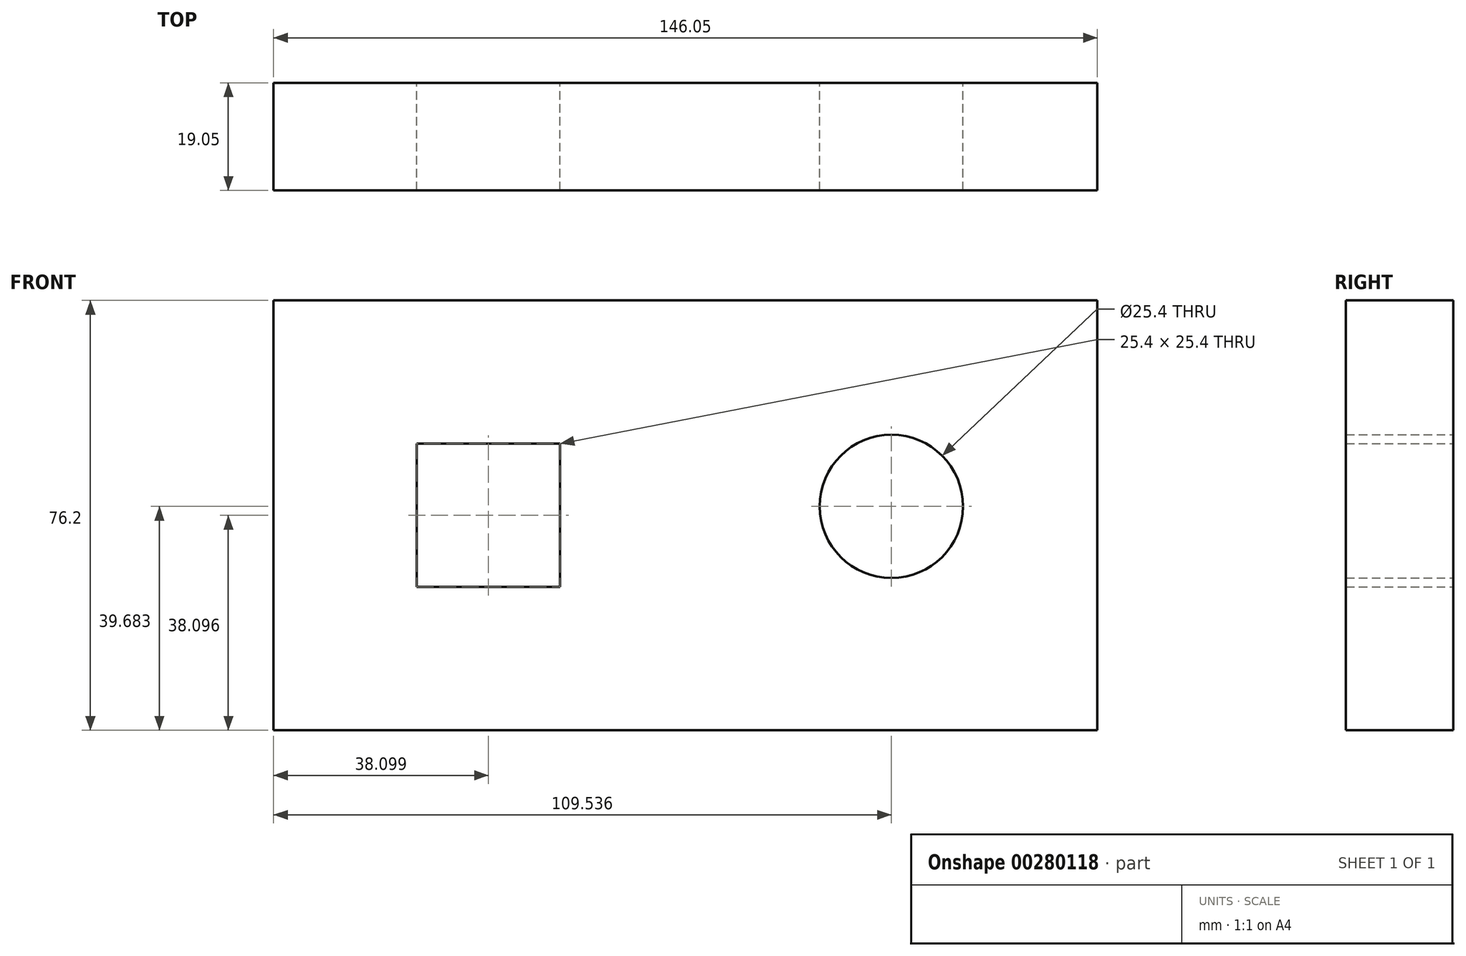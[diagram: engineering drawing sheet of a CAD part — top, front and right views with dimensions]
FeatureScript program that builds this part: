
annotation { "Feature Type Name" : "Feature", "Feature Type Description" : "" }
export const myFeature = defineFeature(function(context is Context, id is Id, definition is map)
    precondition{}
    {
        {
            var Q0;
            Q0=qCreatedBy(makeId("Front.planeOp"),FACE);
            var sketch = newSketch(context, id + "F0", { "sketchPlane" : qUnion([Q0])});
            skLineSegment(sketch, "E0.bottom", {"start": v(-78.26, 55.39) * mm, "end": v(67.79, 55.39) * mm});
            skLineSegment(sketch, "E0.top", {"start": v(-78.26, -20.81) * mm, "end": v(67.79, -20.81) * mm});
            skLineSegment(sketch, "E0.left", {"start": v(-78.26, 55.39) * mm, "end": v(-78.26, -20.81) * mm});
            skLineSegment(sketch, "E0.right", {"start": v(67.79, 55.39) * mm, "end": v(67.79, -20.81) * mm});
            skLineSegment(sketch, "E1.bottom", {"start": v(-27.46, 4.59) * mm, "end": v(-52.86, 4.59) * mm});
            skLineSegment(sketch, "E1.top", {"start": v(-27.46, 29.99) * mm, "end": v(-52.86, 29.99) * mm});
            skLineSegment(sketch, "E1.left", {"start": v(-27.46, 4.59) * mm, "end": v(-27.46, 29.99) * mm});
            skLineSegment(sketch, "E1.right", {"start": v(-52.86, 4.59) * mm, "end": v(-52.86, 29.99) * mm});
            skCircle(sketch, "E2", {"center": v(31.28, 18.87) * mm, "radius": 12.7 * mm});
            skSolve(sketch);
        }
        {
            var Q0;
            Q0=makeQuery(id+"F0.imprint","IMPRINT",FACE,{"disambiguationData":[TD([[makeQuery(id+"F0.imprint","IMPRINT",EDGE,{"derivedFrom":sQuery(id+"F0.wireOp",EDGE,"E0.bottom")}),-1.0]])]});
            extrude(context, id + "F1", {"entities" : qUnion([Q0]), "depth" : 19.05 * mm});
        }
    });
